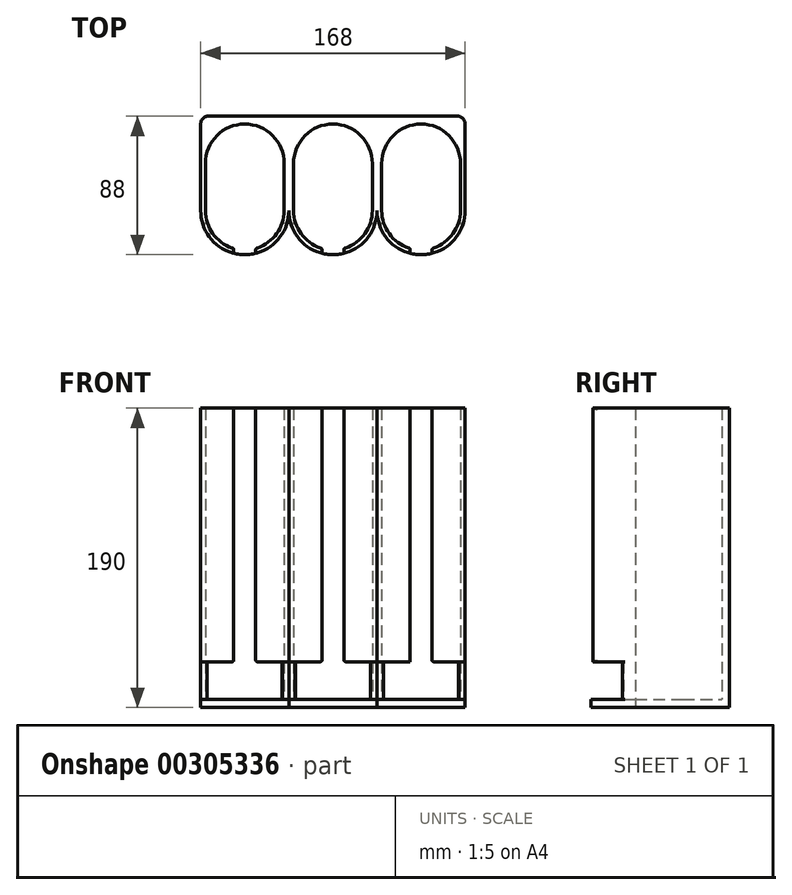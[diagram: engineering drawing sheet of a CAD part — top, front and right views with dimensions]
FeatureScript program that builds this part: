
annotation { "Feature Type Name" : "Feature", "Feature Type Description" : "" }
export const myFeature = defineFeature(function(context is Context, id is Id, definition is map)
    precondition{}
    {
        {
            var Q0;
            Q0=qCreatedBy(makeId("Top.planeOp"),FACE);
            var sketch = newSketch(context, id + "F0", { "sketchPlane" : qUnion([Q0])});
            skArc(sketch, "E0", {"start": v(-34.38, 12.6) * mm, "mid": v(-59.38, 37.6) * mm, "end": v(-84.38, 12.6) * mm});
            skLineSegment(sketch, "E1.left", {"start": v(-84.38, 12.6) * mm, "end": v(-84.38, -17.4) * mm});
            skLineSegment(sketch, "E1.right", {"start": v(-34.38, 12.6) * mm, "end": v(-34.38, -17.4) * mm});
            skArc(sketch, "E2", {"start": v(-84.38, -17.4) * mm, "mid": v(-59.38, -42.4) * mm, "end": v(-34.38, -17.4) * mm});
            skArc(sketch, "E3.2", {"start": v(-87.38, -17.4) * mm, "mid": v(-59.38, -45.4) * mm, "end": v(-31.38, -17.4) * mm});
            skLineSegment(sketch, "E3.3", {"start": v(-87.38, 12.6) * mm, "end": v(-87.38, -17.4) * mm});
            skLineSegment(sketch, "E4.bottom", {"start": v(-66.38, -40.37) * mm, "end": v(-52.38, -40.37) * mm});
            skLineSegment(sketch, "E4.top", {"start": v(-66.38, -47.03) * mm, "end": v(-52.38, -47.03) * mm});
            skLineSegment(sketch, "E4.left", {"start": v(-66.38, -40.37) * mm, "end": v(-66.38, -47.03) * mm});
            skLineSegment(sketch, "E4.right", {"start": v(-52.38, -40.37) * mm, "end": v(-52.38, -47.03) * mm});
            skArc(sketch, "E5", {"start": v(21.62, 12.6) * mm, "mid": v(-3.38, 37.6) * mm, "end": v(-28.38, 12.6) * mm});
            skLineSegment(sketch, "E6.left", {"start": v(-28.38, 12.6) * mm, "end": v(-28.38, -17.4) * mm});
            skLineSegment(sketch, "E6.right", {"start": v(21.62, 12.6) * mm, "end": v(21.62, -17.4) * mm});
            skArc(sketch, "E7", {"start": v(-28.38, -17.4) * mm, "mid": v(-3.38, -42.4) * mm, "end": v(21.62, -17.4) * mm});
            skArc(sketch, "E8.2", {"start": v(-31.38, -17.4) * mm, "mid": v(-3.38, -45.4) * mm, "end": v(24.62, -17.4) * mm});
            skLineSegment(sketch, "E9.bottom", {"start": v(-10.38, -40.37) * mm, "end": v(3.62, -40.37) * mm});
            skLineSegment(sketch, "E9.top", {"start": v(-10.38, -47.03) * mm, "end": v(3.62, -47.03) * mm});
            skLineSegment(sketch, "E9.left", {"start": v(-10.38, -40.37) * mm, "end": v(-10.38, -47.03) * mm});
            skLineSegment(sketch, "E9.right", {"start": v(3.62, -40.37) * mm, "end": v(3.62, -47.03) * mm});
            skArc(sketch, "E10", {"start": v(77.62, 12.6) * mm, "mid": v(52.62, 37.6) * mm, "end": v(27.62, 12.6) * mm});
            skLineSegment(sketch, "E11.left", {"start": v(27.62, 12.6) * mm, "end": v(27.62, -17.4) * mm});
            skLineSegment(sketch, "E11.right", {"start": v(77.62, 12.6) * mm, "end": v(77.62, -17.4) * mm});
            skArc(sketch, "E12", {"start": v(27.62, -17.4) * mm, "mid": v(52.62, -42.4) * mm, "end": v(77.62, -17.4) * mm});
            skLineSegment(sketch, "E13.1", {"start": v(80.62, 12.6) * mm, "end": v(80.62, -17.4) * mm});
            skArc(sketch, "E13.2", {"start": v(24.62, -17.4) * mm, "mid": v(52.62, -45.4) * mm, "end": v(80.62, -17.4) * mm});
            skLineSegment(sketch, "E14.bottom", {"start": v(45.62, -40.37) * mm, "end": v(59.62, -40.37) * mm});
            skLineSegment(sketch, "E14.top", {"start": v(45.62, -47.03) * mm, "end": v(59.62, -47.03) * mm});
            skLineSegment(sketch, "E14.left", {"start": v(45.62, -40.37) * mm, "end": v(45.62, -47.03) * mm});
            skLineSegment(sketch, "E14.right", {"start": v(59.62, -40.37) * mm, "end": v(59.62, -47.03) * mm});
            skLineSegment(sketch, "E15.top", {"start": v(-87.38, 42.6) * mm, "end": v(80.62, 42.6) * mm});
            skLineSegment(sketch, "E15.left", {"start": v(-87.38, 12.6) * mm, "end": v(-87.38, 42.6) * mm});
            skLineSegment(sketch, "E15.right", {"start": v(80.62, 12.6) * mm, "end": v(80.62, 42.6) * mm});
            skSolve(sketch);
        }
        {
            var Q0;
            {var subQ12=sQuery(id+"F0.wireOp",EDGE,"UXST9EkZ-4u4J-23rq-pVFZ-gqdFsX49M8eS.top");Q0=makeQuery(id+"F0.imprint","IMPRINT",FACE,{"disambiguationData":[TD([[makeQuery(id+"F0.imprint","IMPRINT",EDGE,{"derivedFrom":subQ12}),1.0]])]});}
            var Q1;
            {var subQ6=sQuery(id+"F0.wireOp",EDGE,"kwWkXOk3-viDk-uDqX-hwdr-6UO5nTlNDtKJ");Q1=makeQuery(id+"F0.imprint","IMPRINT",FACE,{"disambiguationData":[TD([[makeQuery(id+"F0.imprint","IMPRINT",EDGE,{"derivedFrom":subQ6}),-1.0]])]});}
            var Q2;
            {var subQ0=sQuery(id+"F0.wireOp",EDGE,"kwWkXOk3-viDk-uDqX-hwdr-6UO5nTlNDtKJ");Q2=makeQuery(id+"F0.imprint","IMPRINT",FACE,{"disambiguationData":[TD([[makeQuery(id+"F0.imprint","IMPRINT",EDGE,{"derivedFrom":subQ0}),1.0]])]});}
            var Q3;
            {var subQ5=sQuery(id+"F0.wireOp",EDGE,"a4c4f6ce-adb7-4228-82a1-ecae965dd3bb.0");var subQ7=sQuery(id+"F0.wireOp",EDGE,"a4c4f6ce-adb7-4228-82a1-ecae965dd3bb.3");var subQ8=makeQuery(id+"F0.imprint","INTERSECT",VERTEX,{"derivedFrom":[subQ5,subQ7]});Q3=makeQuery(id+"F0.imprint","IMPRINT",FACE,{"disambiguationData":[TD([[makeQuery(id+"F0.imprint","IMPRINT",EDGE,{"disambiguationData":[TD([[subQ8,1.0]])],"derivedFrom":subQ5}),1.0]])]});}
            var Q4;
            {var subQ8=sQuery(id+"F0.wireOp",EDGE,"a4c4f6ce-adb7-4228-82a1-ecae965dd3bb.0");var subQ11=sQuery(id+"F0.wireOp",EDGE,"a4c4f6ce-adb7-4228-82a1-ecae965dd3bb.3");var subQ12=makeQuery(id+"F0.imprint","INTERSECT",VERTEX,{"derivedFrom":[subQ8,subQ11]});Q4=makeQuery(id+"F0.imprint","IMPRINT",FACE,{"disambiguationData":[TD([[makeQuery(id+"F0.imprint","IMPRINT",EDGE,{"disambiguationData":[TD([[subQ12,1.0]])],"derivedFrom":subQ8}),-1.0]])]});}
            var Q5;
            {var subQ0=sQuery(id+"F0.wireOp",EDGE,"96b1cbd4-130d-4a2d-9362-919a265e6331.right");var subQ1=sQuery(id+"F0.wireOp",EDGE,"45cc61fa-5a03-413e-84e5-3475a93230b5");var subQ2=makeQuery(id+"F0.imprint","INTERSECT",VERTEX,{"derivedFrom":[subQ1,subQ0]});Q5=makeQuery(id+"F0.imprint","IMPRINT",FACE,{"disambiguationData":[TD([[makeQuery(id+"F0.imprint","IMPRINT",EDGE,{"disambiguationData":[TD([[subQ2,-1.0]])],"derivedFrom":subQ1}),1.0]])]});}
            var Q6;
            {var subQ5=sQuery(id+"F0.wireOp",EDGE,"E3.0");var subQ6=sQuery(id+"F0.wireOp",EDGE,"45cc61fa-5a03-413e-84e5-3475a93230b5");var subQ7=makeQuery(id+"F0.imprint","INTERSECT",VERTEX,{"derivedFrom":[subQ6,subQ5]});Q6=makeQuery(id+"F0.imprint","IMPRINT",FACE,{"disambiguationData":[TD([[makeQuery(id+"F0.imprint","IMPRINT",EDGE,{"disambiguationData":[TD([[subQ7,-1.0]])],"derivedFrom":subQ6}),-1.0]])]});}
            var Q7;
            {var subQ0=sQuery(id+"F0.wireOp",EDGE,"E0");var subQ1=sQuery(id+"F0.wireOp",EDGE,"855d7c93-3dc1-4a9f-ad3a-edb05c3c6de2.0");var subQ2=makeQuery(id+"F0.imprint","INTERSECT",VERTEX,{"derivedFrom":[subQ1,subQ0]});Q7=makeQuery(id+"F0.imprint","IMPRINT",FACE,{"disambiguationData":[TD([[makeQuery(id+"F0.imprint","IMPRINT",EDGE,{"disambiguationData":[TD([[subQ2,-1.0]])],"derivedFrom":subQ1}),-1.0]])]});}
            var Q8;
            {var subQ3=sQuery(id+"F0.wireOp",EDGE,"855d7c93-3dc1-4a9f-ad3a-edb05c3c6de2.0");var subQ6=sQuery(id+"F0.wireOp",EDGE,"E3.0");var subQ8=makeQuery(id+"F0.imprint","INTERSECT",VERTEX,{"derivedFrom":[subQ3,subQ6]});Q8=makeQuery(id+"F0.imprint","IMPRINT",FACE,{"disambiguationData":[TD([[makeQuery(id+"F0.imprint","IMPRINT",EDGE,{"disambiguationData":[TD([[subQ8,-1.0]])],"derivedFrom":subQ3}),-1.0]])]});}
            var Q9;
            {var subQ1=sQuery(id+"F0.wireOp",EDGE,"96b1cbd4-130d-4a2d-9362-919a265e6331.left");Q9=makeQuery(id+"F0.imprint","IMPRINT",FACE,{"disambiguationData":[TD([[makeQuery(id+"F0.imprint","IMPRINT",EDGE,{"derivedFrom":subQ1}),-1.0]])]});}
            var Q10;
            {var subQ7=sQuery(id+"F0.wireOp",EDGE,"E2");var subQ8=sQuery(id+"F0.wireOp",EDGE,"E1.left");var subQ9=makeQuery(id+"F0.imprint","INTERSECT",VERTEX,{"derivedFrom":[subQ8,subQ7]});Q10=makeQuery(id+"F0.imprint","IMPRINT",FACE,{"disambiguationData":[TD([[makeQuery(id+"F0.imprint","IMPRINT",EDGE,{"disambiguationData":[TD([[subQ9,1.0]])],"derivedFrom":subQ8}),-1.0]])]});}
            var Q11;
            {var subQ10=sQuery(id+"F0.wireOp",EDGE,"855d7c93-3dc1-4a9f-ad3a-edb05c3c6de2.3");Q11=makeQuery(id+"F0.imprint","IMPRINT",FACE,{"disambiguationData":[TD([[makeQuery(id+"F0.imprint","IMPRINT",EDGE,{"derivedFrom":subQ10}),-1.0]])]});}
            var Q12;
            {var subQ5=sQuery(id+"F0.wireOp",EDGE,"E4.bottom");Q12=makeQuery(id+"F0.imprint","IMPRINT",FACE,{"disambiguationData":[TD([[makeQuery(id+"F0.imprint","IMPRINT",EDGE,{"derivedFrom":subQ5}),-1.0]])]});}
            var Q13;
            {var subQ0=sQuery(id+"F0.wireOp",EDGE,"E3.2");var subQ1=sQuery(id+"F0.wireOp",EDGE,"855d7c93-3dc1-4a9f-ad3a-edb05c3c6de2.2");var subQ2=makeQuery(id+"F0.imprint","INTERSECT",VERTEX,{"derivedFrom":[subQ1,subQ0]});Q13=makeQuery(id+"F0.imprint","IMPRINT",FACE,{"disambiguationData":[TD([[makeQuery(id+"F0.imprint","IMPRINT",EDGE,{"disambiguationData":[TD([[subQ2,1.0]])],"derivedFrom":subQ1}),-1.0]])]});}
            var Q14;
            {var subQ6=sQuery(id+"F0.wireOp",EDGE,"o4JAiXg9-DfQB-Lprr-swcd-07qpl5tI4RPW.bottom");Q14=makeQuery(id+"F0.imprint","IMPRINT",FACE,{"disambiguationData":[TD([[makeQuery(id+"F0.imprint","IMPRINT",EDGE,{"derivedFrom":subQ6}),1.0]])]});}
            var Q15;
            {var subQ1=sQuery(id+"F0.wireOp",EDGE,"E3.1");var subQ5=sQuery(id+"F0.wireOp",EDGE,"d6663e3e-9dfa-41b2-b02d-e6aec3a7e438");var subQ6=makeQuery(id+"F0.imprint","INTERSECT",VERTEX,{"derivedFrom":[subQ5,subQ1]});Q15=makeQuery(id+"F0.imprint","IMPRINT",FACE,{"disambiguationData":[TD([[makeQuery(id+"F0.imprint","IMPRINT",EDGE,{"disambiguationData":[TD([[subQ6,-1.0]])],"derivedFrom":subQ5}),-1.0]])]});}
            var Q16;
            {var subQ5=sQuery(id+"F0.wireOp",EDGE,"o4JAiXg9-DfQB-Lprr-swcd-07qpl5tI4RPW.bottom");Q16=makeQuery(id+"F0.imprint","IMPRINT",FACE,{"disambiguationData":[TD([[makeQuery(id+"F0.imprint","IMPRINT",EDGE,{"derivedFrom":subQ5}),-1.0]])]});}
            var Q17;
            {var subQ0=sQuery(id+"F0.wireOp",EDGE,"o4JAiXg9-DfQB-Lprr-swcd-07qpl5tI4RPW.left");var subQ1=sQuery(id+"F0.wireOp",EDGE,"d6663e3e-9dfa-41b2-b02d-e6aec3a7e438");var subQ2=makeQuery(id+"F0.imprint","INTERSECT",VERTEX,{"derivedFrom":[subQ1,subQ0]});Q17=makeQuery(id+"F0.imprint","IMPRINT",FACE,{"disambiguationData":[TD([[makeQuery(id+"F0.imprint","IMPRINT",EDGE,{"disambiguationData":[TD([[subQ2,-1.0]])],"derivedFrom":subQ1}),-1.0]])]});}
            var Q18;
            {var subQ5=sQuery(id+"F0.wireOp",EDGE,"a4c4f6ce-adb7-4228-82a1-ecae965dd3bb.3");var subQ6=sQuery(id+"F0.wireOp",EDGE,"a4c4f6ce-adb7-4228-82a1-ecae965dd3bb.2");var subQ7=makeQuery(id+"F0.imprint","INTERSECT",VERTEX,{"derivedFrom":[subQ6,subQ5]});Q18=makeQuery(id+"F0.imprint","IMPRINT",FACE,{"disambiguationData":[TD([[makeQuery(id+"F0.imprint","IMPRINT",EDGE,{"disambiguationData":[TD([[subQ7,-1.0]])],"derivedFrom":subQ6}),-1.0]])]});}
            var Q19;
            {var subQ3=sQuery(id+"F0.wireOp",EDGE,"a4c4f6ce-adb7-4228-82a1-ecae965dd3bb.2");var subQ7=sQuery(id+"F0.wireOp",EDGE,"a4c4f6ce-adb7-4228-82a1-ecae965dd3bb.3");var subQ8=makeQuery(id+"F0.imprint","INTERSECT",VERTEX,{"derivedFrom":[subQ3,subQ7]});Q19=makeQuery(id+"F0.imprint","IMPRINT",FACE,{"disambiguationData":[TD([[makeQuery(id+"F0.imprint","IMPRINT",EDGE,{"disambiguationData":[TD([[subQ8,-1.0]])],"derivedFrom":subQ3}),1.0]])]});}
            var Q20;
            {var subQ5=sQuery(id+"F0.wireOp",EDGE,"zHXG1qvy-AbRm-SIj7-NfRi-9Sy5astTL28w");var subQ6=sQuery(id+"F0.wireOp",EDGE,"nXfFn5N0-6Buh-Se6b-7rvE-6La1GT5WE5c2.left");var subQ7=makeQuery(id+"F0.imprint","INTERSECT",VERTEX,{"derivedFrom":[subQ6,subQ5]});Q20=makeQuery(id+"F0.imprint","IMPRINT",FACE,{"disambiguationData":[TD([[makeQuery(id+"F0.imprint","IMPRINT",EDGE,{"disambiguationData":[TD([[subQ7,1.0]])],"derivedFrom":subQ6}),-1.0]])]});}
            var Q21;
            {var subQ0=sQuery(id+"F0.wireOp",EDGE,"kCUj0TKU-8dMh-rkvJ-Fl4E-ZpoXySVFhUaY.left");var subQ1=sQuery(id+"F0.wireOp",EDGE,"zHXG1qvy-AbRm-SIj7-NfRi-9Sy5astTL28w");var subQ2=makeQuery(id+"F0.imprint","INTERSECT",VERTEX,{"derivedFrom":[subQ1,subQ0]});Q21=makeQuery(id+"F0.imprint","IMPRINT",FACE,{"disambiguationData":[TD([[makeQuery(id+"F0.imprint","IMPRINT",EDGE,{"disambiguationData":[TD([[subQ2,-1.0]])],"derivedFrom":subQ1}),-1.0]])]});}
            var Q22;
            {var subQ0=sQuery(id+"F0.wireOp",EDGE,"a4c4f6ce-adb7-4228-82a1-ecae965dd3bb.1");Q22=makeQuery(id+"F0.imprint","IMPRINT",FACE,{"disambiguationData":[TD([[makeQuery(id+"F0.imprint","IMPRINT",EDGE,{"derivedFrom":subQ0}),-1.0]])]});}
            var Q23;
            {var subQ9=sQuery(id+"F0.wireOp",EDGE,"kCUj0TKU-8dMh-rkvJ-Fl4E-ZpoXySVFhUaY.bottom");Q23=makeQuery(id+"F0.imprint","IMPRINT",FACE,{"disambiguationData":[TD([[makeQuery(id+"F0.imprint","IMPRINT",EDGE,{"derivedFrom":subQ9}),1.0]])]});}
            var Q24;
            {var subQ5=sQuery(id+"F0.wireOp",EDGE,"kCUj0TKU-8dMh-rkvJ-Fl4E-ZpoXySVFhUaY.bottom");Q24=makeQuery(id+"F0.imprint","IMPRINT",FACE,{"disambiguationData":[TD([[makeQuery(id+"F0.imprint","IMPRINT",EDGE,{"derivedFrom":subQ5}),-1.0]])]});}
            var Q25;
            {var subQ0=sQuery(id+"F0.wireOp",EDGE,"E0");Q25=makeQuery(id+"F0.imprint","IMPRINT",FACE,{"disambiguationData":[TD([[makeQuery(id+"F0.imprint","IMPRINT",EDGE,{"derivedFrom":subQ0}),-1.0]])]});}
            var Q26;
            {var subQ5=sQuery(id+"F0.wireOp",EDGE,"E1.right");Q26=makeQuery(id+"F0.imprint","IMPRINT",FACE,{"disambiguationData":[TD([[makeQuery(id+"F0.imprint","IMPRINT",EDGE,{"derivedFrom":subQ5}),1.0]])]});}
            var Q27;
            {var subQ5=sQuery(id+"F0.wireOp",EDGE,"E6.left");Q27=makeQuery(id+"F0.imprint","IMPRINT",FACE,{"disambiguationData":[TD([[makeQuery(id+"F0.imprint","IMPRINT",EDGE,{"derivedFrom":subQ5}),-1.0]])]});}
            var Q28;
            {var subQ0=sQuery(id+"F0.wireOp",EDGE,"E5");Q28=makeQuery(id+"F0.imprint","IMPRINT",FACE,{"disambiguationData":[TD([[makeQuery(id+"F0.imprint","IMPRINT",EDGE,{"derivedFrom":subQ0}),-1.0]])]});}
            var Q29;
            {var subQ5=sQuery(id+"F0.wireOp",EDGE,"E6.right");Q29=makeQuery(id+"F0.imprint","IMPRINT",FACE,{"disambiguationData":[TD([[makeQuery(id+"F0.imprint","IMPRINT",EDGE,{"derivedFrom":subQ5}),1.0]])]});}
            var Q30;
            {var subQ5=sQuery(id+"F0.wireOp",EDGE,"E11.left");Q30=makeQuery(id+"F0.imprint","IMPRINT",FACE,{"disambiguationData":[TD([[makeQuery(id+"F0.imprint","IMPRINT",EDGE,{"derivedFrom":subQ5}),-1.0]])]});}
            var Q31;
            {var subQ0=sQuery(id+"F0.wireOp",EDGE,"E10");Q31=makeQuery(id+"F0.imprint","IMPRINT",FACE,{"disambiguationData":[TD([[makeQuery(id+"F0.imprint","IMPRINT",EDGE,{"derivedFrom":subQ0}),-1.0]])]});}
            var Q32;
            {var subQ5=sQuery(id+"F0.wireOp",EDGE,"E11.right");Q32=makeQuery(id+"F0.imprint","IMPRINT",FACE,{"disambiguationData":[TD([[makeQuery(id+"F0.imprint","IMPRINT",EDGE,{"derivedFrom":subQ5}),1.0]])]});}
            var Q33;
            {var subQ0=sQuery(id+"F0.wireOp",EDGE,"E4.left");var subQ1=sQuery(id+"F0.wireOp",EDGE,"E2");var subQ2=makeQuery(id+"F0.imprint","INTERSECT",VERTEX,{"derivedFrom":[subQ1,subQ0]});Q33=makeQuery(id+"F0.imprint","IMPRINT",FACE,{"disambiguationData":[TD([[makeQuery(id+"F0.imprint","IMPRINT",EDGE,{"disambiguationData":[TD([[subQ2,-1.0]])],"derivedFrom":subQ1}),-1.0]])]});}
            var Q34;
            {var subQ7=sQuery(id+"F0.wireOp",EDGE,"E1.left");Q34=makeQuery(id+"F0.imprint","IMPRINT",FACE,{"disambiguationData":[TD([[makeQuery(id+"F0.imprint","IMPRINT",EDGE,{"derivedFrom":subQ7}),1.0]])]});}
            var Q35;
            {var subQ4=sQuery(id+"F0.wireOp",EDGE,"E6.left");Q35=makeQuery(id+"F0.imprint","IMPRINT",FACE,{"disambiguationData":[TD([[makeQuery(id+"F0.imprint","IMPRINT",EDGE,{"derivedFrom":subQ4}),1.0]])]});}
            var Q36;
            {var subQ5=sQuery(id+"F0.wireOp",EDGE,"E9.bottom");Q36=makeQuery(id+"F0.imprint","IMPRINT",FACE,{"disambiguationData":[TD([[makeQuery(id+"F0.imprint","IMPRINT",EDGE,{"derivedFrom":subQ5}),-1.0]])]});}
            var Q37;
            {var subQ0=sQuery(id+"F0.wireOp",EDGE,"E9.left");var subQ1=sQuery(id+"F0.wireOp",EDGE,"E7");var subQ2=makeQuery(id+"F0.imprint","INTERSECT",VERTEX,{"derivedFrom":[subQ1,subQ0]});Q37=makeQuery(id+"F0.imprint","IMPRINT",FACE,{"disambiguationData":[TD([[makeQuery(id+"F0.imprint","IMPRINT",EDGE,{"disambiguationData":[TD([[subQ2,-1.0]])],"derivedFrom":subQ1}),-1.0]])]});}
            var Q38;
            {var subQ0=sQuery(id+"F0.wireOp",EDGE,"E0");Q38=makeQuery(id+"F0.imprint","IMPRINT",FACE,{"disambiguationData":[TD([[makeQuery(id+"F0.imprint","IMPRINT",EDGE,{"derivedFrom":subQ0}),1.0]])]});}
            var Q39;
            {var subQ0=sQuery(id+"F0.wireOp",EDGE,"E5");Q39=makeQuery(id+"F0.imprint","IMPRINT",FACE,{"disambiguationData":[TD([[makeQuery(id+"F0.imprint","IMPRINT",EDGE,{"derivedFrom":subQ0}),1.0]])]});}
            var Q40;
            {var subQ0=sQuery(id+"F0.wireOp",EDGE,"E10");Q40=makeQuery(id+"F0.imprint","IMPRINT",FACE,{"disambiguationData":[TD([[makeQuery(id+"F0.imprint","IMPRINT",EDGE,{"derivedFrom":subQ0}),1.0]])]});}
            var Q41;
            {var subQ4=sQuery(id+"F0.wireOp",EDGE,"E11.left");Q41=makeQuery(id+"F0.imprint","IMPRINT",FACE,{"disambiguationData":[TD([[makeQuery(id+"F0.imprint","IMPRINT",EDGE,{"derivedFrom":subQ4}),1.0]])]});}
            var Q42;
            {var subQ5=sQuery(id+"F0.wireOp",EDGE,"E14.bottom");Q42=makeQuery(id+"F0.imprint","IMPRINT",FACE,{"disambiguationData":[TD([[makeQuery(id+"F0.imprint","IMPRINT",EDGE,{"derivedFrom":subQ5}),-1.0]])]});}
            var Q43;
            {var subQ0=sQuery(id+"F0.wireOp",EDGE,"E14.left");var subQ1=sQuery(id+"F0.wireOp",EDGE,"E12");var subQ2=makeQuery(id+"F0.imprint","INTERSECT",VERTEX,{"derivedFrom":[subQ1,subQ0]});Q43=makeQuery(id+"F0.imprint","IMPRINT",FACE,{"disambiguationData":[TD([[makeQuery(id+"F0.imprint","IMPRINT",EDGE,{"disambiguationData":[TD([[subQ2,-1.0]])],"derivedFrom":subQ1}),-1.0]])]});}
            extrude(context, id + "F1", {"entities" : qUnion([Q0, Q1, Q2, Q3, Q4, Q5, Q6, Q7, Q8, Q9, Q10, Q11, Q12, Q13, Q14, Q15, Q16, Q17, Q18, Q19, Q20, Q21, Q22, Q23, Q24, Q25, Q26, Q27, Q28, Q29, Q30, Q31, Q32, Q33, Q34, Q35, Q36, Q37, Q38, Q39, Q40, Q41, Q42, Q43]), "depth" : 5 * mm});
        }
        {
            var Q0;
            {var subQ0=sQuery(id+"F0.wireOp",EDGE,"a4c4f6ce-adb7-4228-82a1-ecae965dd3bb.1");Q0=makeQuery(id+"F0.imprint","IMPRINT",FACE,{"disambiguationData":[TD([[makeQuery(id+"F0.imprint","IMPRINT",EDGE,{"derivedFrom":subQ0}),-1.0]])]});}
            var Q1;
            {var subQ6=sQuery(id+"F0.wireOp",EDGE,"kwWkXOk3-viDk-uDqX-hwdr-6UO5nTlNDtKJ");Q1=makeQuery(id+"F0.imprint","IMPRINT",FACE,{"disambiguationData":[TD([[makeQuery(id+"F0.imprint","IMPRINT",EDGE,{"derivedFrom":subQ6}),-1.0]])]});}
            var Q2;
            {var subQ5=sQuery(id+"F0.wireOp",EDGE,"zHXG1qvy-AbRm-SIj7-NfRi-9Sy5astTL28w");var subQ6=sQuery(id+"F0.wireOp",EDGE,"nXfFn5N0-6Buh-Se6b-7rvE-6La1GT5WE5c2.left");var subQ7=makeQuery(id+"F0.imprint","INTERSECT",VERTEX,{"derivedFrom":[subQ6,subQ5]});Q2=makeQuery(id+"F0.imprint","IMPRINT",FACE,{"disambiguationData":[TD([[makeQuery(id+"F0.imprint","IMPRINT",EDGE,{"disambiguationData":[TD([[subQ7,1.0]])],"derivedFrom":subQ6}),-1.0]])]});}
            var Q3;
            {var subQ5=sQuery(id+"F0.wireOp",EDGE,"a4c4f6ce-adb7-4228-82a1-ecae965dd3bb.3");var subQ6=sQuery(id+"F0.wireOp",EDGE,"a4c4f6ce-adb7-4228-82a1-ecae965dd3bb.2");var subQ7=makeQuery(id+"F0.imprint","INTERSECT",VERTEX,{"derivedFrom":[subQ6,subQ5]});Q3=makeQuery(id+"F0.imprint","IMPRINT",FACE,{"disambiguationData":[TD([[makeQuery(id+"F0.imprint","IMPRINT",EDGE,{"disambiguationData":[TD([[subQ7,-1.0]])],"derivedFrom":subQ6}),-1.0]])]});}
            var Q4;
            {var subQ3=sQuery(id+"F0.wireOp",EDGE,"a4c4f6ce-adb7-4228-82a1-ecae965dd3bb.2");var subQ7=sQuery(id+"F0.wireOp",EDGE,"a4c4f6ce-adb7-4228-82a1-ecae965dd3bb.3");var subQ8=makeQuery(id+"F0.imprint","INTERSECT",VERTEX,{"derivedFrom":[subQ3,subQ7]});Q4=makeQuery(id+"F0.imprint","IMPRINT",FACE,{"disambiguationData":[TD([[makeQuery(id+"F0.imprint","IMPRINT",EDGE,{"disambiguationData":[TD([[subQ8,-1.0]])],"derivedFrom":subQ3}),1.0]])]});}
            var Q5;
            {var subQ5=sQuery(id+"F0.wireOp",EDGE,"a4c4f6ce-adb7-4228-82a1-ecae965dd3bb.0");var subQ7=sQuery(id+"F0.wireOp",EDGE,"a4c4f6ce-adb7-4228-82a1-ecae965dd3bb.3");var subQ8=makeQuery(id+"F0.imprint","INTERSECT",VERTEX,{"derivedFrom":[subQ5,subQ7]});Q5=makeQuery(id+"F0.imprint","IMPRINT",FACE,{"disambiguationData":[TD([[makeQuery(id+"F0.imprint","IMPRINT",EDGE,{"disambiguationData":[TD([[subQ8,1.0]])],"derivedFrom":subQ5}),1.0]])]});}
            var Q6;
            {var subQ8=sQuery(id+"F0.wireOp",EDGE,"a4c4f6ce-adb7-4228-82a1-ecae965dd3bb.0");var subQ11=sQuery(id+"F0.wireOp",EDGE,"a4c4f6ce-adb7-4228-82a1-ecae965dd3bb.3");var subQ12=makeQuery(id+"F0.imprint","INTERSECT",VERTEX,{"derivedFrom":[subQ8,subQ11]});Q6=makeQuery(id+"F0.imprint","IMPRINT",FACE,{"disambiguationData":[TD([[makeQuery(id+"F0.imprint","IMPRINT",EDGE,{"disambiguationData":[TD([[subQ12,1.0]])],"derivedFrom":subQ8}),-1.0]])]});}
            var Q7;
            {var subQ1=sQuery(id+"F0.wireOp",EDGE,"E3.1");var subQ5=sQuery(id+"F0.wireOp",EDGE,"d6663e3e-9dfa-41b2-b02d-e6aec3a7e438");var subQ6=makeQuery(id+"F0.imprint","INTERSECT",VERTEX,{"derivedFrom":[subQ5,subQ1]});Q7=makeQuery(id+"F0.imprint","IMPRINT",FACE,{"disambiguationData":[TD([[makeQuery(id+"F0.imprint","IMPRINT",EDGE,{"disambiguationData":[TD([[subQ6,-1.0]])],"derivedFrom":subQ5}),-1.0]])]});}
            var Q8;
            {var subQ1=sQuery(id+"F0.wireOp",EDGE,"96b1cbd4-130d-4a2d-9362-919a265e6331.left");Q8=makeQuery(id+"F0.imprint","IMPRINT",FACE,{"disambiguationData":[TD([[makeQuery(id+"F0.imprint","IMPRINT",EDGE,{"derivedFrom":subQ1}),-1.0]])]});}
            var Q9;
            {var subQ0=sQuery(id+"F0.wireOp",EDGE,"E3.2");var subQ1=sQuery(id+"F0.wireOp",EDGE,"855d7c93-3dc1-4a9f-ad3a-edb05c3c6de2.2");var subQ2=makeQuery(id+"F0.imprint","INTERSECT",VERTEX,{"derivedFrom":[subQ1,subQ0]});Q9=makeQuery(id+"F0.imprint","IMPRINT",FACE,{"disambiguationData":[TD([[makeQuery(id+"F0.imprint","IMPRINT",EDGE,{"disambiguationData":[TD([[subQ2,1.0]])],"derivedFrom":subQ1}),-1.0]])]});}
            var Q10;
            {var subQ5=sQuery(id+"F0.wireOp",EDGE,"E3.0");var subQ6=sQuery(id+"F0.wireOp",EDGE,"45cc61fa-5a03-413e-84e5-3475a93230b5");var subQ7=makeQuery(id+"F0.imprint","INTERSECT",VERTEX,{"derivedFrom":[subQ6,subQ5]});Q10=makeQuery(id+"F0.imprint","IMPRINT",FACE,{"disambiguationData":[TD([[makeQuery(id+"F0.imprint","IMPRINT",EDGE,{"disambiguationData":[TD([[subQ7,-1.0]])],"derivedFrom":subQ6}),-1.0]])]});}
            var Q11;
            {var subQ3=sQuery(id+"F0.wireOp",EDGE,"855d7c93-3dc1-4a9f-ad3a-edb05c3c6de2.0");var subQ6=sQuery(id+"F0.wireOp",EDGE,"E3.0");var subQ8=makeQuery(id+"F0.imprint","INTERSECT",VERTEX,{"derivedFrom":[subQ3,subQ6]});Q11=makeQuery(id+"F0.imprint","IMPRINT",FACE,{"disambiguationData":[TD([[makeQuery(id+"F0.imprint","IMPRINT",EDGE,{"disambiguationData":[TD([[subQ8,-1.0]])],"derivedFrom":subQ3}),-1.0]])]});}
            var Q12;
            {var subQ7=sQuery(id+"F0.wireOp",EDGE,"E2");var subQ8=sQuery(id+"F0.wireOp",EDGE,"E1.left");var subQ9=makeQuery(id+"F0.imprint","INTERSECT",VERTEX,{"derivedFrom":[subQ8,subQ7]});Q12=makeQuery(id+"F0.imprint","IMPRINT",FACE,{"disambiguationData":[TD([[makeQuery(id+"F0.imprint","IMPRINT",EDGE,{"disambiguationData":[TD([[subQ9,1.0]])],"derivedFrom":subQ8}),-1.0]])]});}
            var Q13;
            {var subQ12=sQuery(id+"F0.wireOp",EDGE,"UXST9EkZ-4u4J-23rq-pVFZ-gqdFsX49M8eS.top");Q13=makeQuery(id+"F0.imprint","IMPRINT",FACE,{"disambiguationData":[TD([[makeQuery(id+"F0.imprint","IMPRINT",EDGE,{"derivedFrom":subQ12}),1.0]])]});}
            extrude(context, id + "F2", {"entities" : qUnion([Q0, Q1, Q2, Q3, Q4, Q5, Q6, Q7, Q8, Q9, Q10, Q11, Q12, Q13]), "operationType" : NewBodyOperationType.ADD, "depth" : 190 * mm});
        }
        {
            var Q0;
            Q0=qCreatedBy(makeId("Front.planeOp"),FACE);
            cPlane(context, id + "F3", {"entities" : qUnion([Q0]), "cplaneType" : CPlaneType.OFFSET, "offset" : 50 * mm, "width" : 150 * mm, "height" : 150 * mm});
        }
        {
            var Q0;
            Q0=qCreatedBy(id+"F3.planeOp",FACE);
            var sketch = newSketch(context, id + "F4", { "sketchPlane" : qUnion([Q0])});
            skLineSegment(sketch, "E16.bottom", {"start": v(-83.38, 29) * mm, "end": v(-35.38, 29) * mm});
            skLineSegment(sketch, "E16.top", {"start": v(-83.38, 5) * mm, "end": v(-35.38, 5) * mm});
            skLineSegment(sketch, "E16.left", {"start": v(-83.38, 29) * mm, "end": v(-83.38, 5) * mm});
            skLineSegment(sketch, "E16.right", {"start": v(-35.38, 29) * mm, "end": v(-35.38, 5) * mm});
            skLineSegment(sketch, "E17.bottom", {"start": v(20.62, 29) * mm, "end": v(-27.38, 29) * mm});
            skLineSegment(sketch, "E17.top", {"start": v(20.62, 5) * mm, "end": v(-27.38, 5) * mm});
            skLineSegment(sketch, "E17.left", {"start": v(-27.38, 29) * mm, "end": v(-27.38, 5) * mm});
            skLineSegment(sketch, "E17.right", {"start": v(20.62, 29) * mm, "end": v(20.62, 5) * mm});
            skLineSegment(sketch, "E18.bottom", {"start": v(28.62, 29) * mm, "end": v(76.62, 29) * mm});
            skLineSegment(sketch, "E18.top", {"start": v(28.62, 5) * mm, "end": v(76.62, 5) * mm});
            skLineSegment(sketch, "E18.left", {"start": v(28.62, 29) * mm, "end": v(28.62, 5) * mm});
            skLineSegment(sketch, "E18.right", {"start": v(76.62, 29) * mm, "end": v(76.62, 5) * mm});
            skSolve(sketch);
        }
        {
            var Q0;
            Q0=makeQuery(id+"F4.imprint","IMPRINT",FACE,{"disambiguationData":[TD([[makeQuery(id+"F4.imprint","IMPRINT",EDGE,{"derivedFrom":sQuery(id+"F4.wireOp",EDGE,"E16.bottom")}),-1.0]])]});
            var Q1;
            Q1=makeQuery(id+"F4.imprint","IMPRINT",FACE,{"disambiguationData":[TD([[makeQuery(id+"F4.imprint","IMPRINT",EDGE,{"derivedFrom":sQuery(id+"F4.wireOp",EDGE,"E17.bottom")}),1.0]])]});
            var Q2;
            Q2=makeQuery(id+"F4.imprint","IMPRINT",FACE,{"disambiguationData":[TD([[makeQuery(id+"F4.imprint","IMPRINT",EDGE,{"derivedFrom":sQuery(id+"F4.wireOp",EDGE,"E18.bottom")}),-1.0]])]});
            extrude(context, id + "F5", {"entities" : qUnion([Q0, Q1, Q2]), "operationType" : NewBodyOperationType.REMOVE, "oppositeDirection" : true, "depth" : 25 * mm});
        }
        {
            var Q0;
            {var subQ0=sQuery(id+"F0.wireOp",EDGE,"E15.left");var subQ1=sQuery(id+"F0.wireOp",EDGE,"E15.top");Q0=makeQuery(id+"F2.boolean.opBoolean","MERGE",EDGE,{"derivedFrom":[makeQuery(id+"F1.opExtrude","SWEPT_EDGE",EDGE,{"disambiguationData":[OSD([subQ1,subQ0])]}),makeQuery(id+"F2.opExtrude","SWEPT_EDGE",EDGE,{"disambiguationData":[OSD([subQ1,subQ0])]})]});}
            var Q1;
            {var subQ0=sQuery(id+"F0.wireOp",EDGE,"E15.right");var subQ1=sQuery(id+"F0.wireOp",EDGE,"E15.top");Q1=makeQuery(id+"F2.boolean.opBoolean","MERGE",EDGE,{"derivedFrom":[makeQuery(id+"F1.opExtrude","SWEPT_EDGE",EDGE,{"disambiguationData":[OSD([subQ1,subQ0])]}),makeQuery(id+"F2.opExtrude","SWEPT_EDGE",EDGE,{"disambiguationData":[OSD([subQ1,subQ0])]})]});}
            fillet(context, id + "F6", {"entities" : qUnion([Q0, Q1]), "radius" : 5 * mm, "tangentPropagation" : true, "allowEdgeOverflow" : false});
        }
        {
            var Q0;
            {var subQ0=sQuery(id+"F0.wireOp",EDGE,"E3.2");Q0=makeQuery(id+"F5.boolean.opBoolean","INTERSECT",EDGE,{"derivedFrom":[makeQuery(id+"F2.boolean.opBoolean","MERGE",FACE,{"derivedFrom":[makeQuery(id+"F1.opExtrude","SWEPT_FACE",FACE,{"disambiguationData":[OSD([subQ0])]}),makeQuery(id+"F2.opExtrude","SWEPT_FACE",FACE,{"disambiguationData":[OSD([subQ0]),TDD([makeQuery(id+"F0.imprint","IMPRINT",EDGE,{"disambiguationData":[TD([[makeQuery(id+"F0.imprint","INTERSECT",VERTEX,{"derivedFrom":[subQ0,sQuery(id+"F0.wireOp",EDGE,"E3.3")]}),-1.0]])],"derivedFrom":subQ0})])]}),makeQuery(id+"F2.opExtrude","SWEPT_FACE",FACE,{"disambiguationData":[OSD([subQ0]),TDD([makeQuery(id+"F0.imprint","IMPRINT",EDGE,{"disambiguationData":[TD([[makeQuery(id+"F0.imprint","INTERSECT",VERTEX,{"derivedFrom":[subQ0,sQuery(id+"F0.wireOp",EDGE,"E8.2")]}),1.0]])],"derivedFrom":subQ0})])]})]}),makeQuery(id+"F5.opExtrude","SWEPT_FACE",FACE,{"disambiguationData":[OSD([sQuery(id+"F4.wireOp",EDGE,"E16.left")])]})]});}
            var Q1;
            {var subQ0=sQuery(id+"F0.wireOp",EDGE,"E3.2");Q1=makeQuery(id+"F5.boolean.opBoolean","INTERSECT",EDGE,{"derivedFrom":[makeQuery(id+"F2.boolean.opBoolean","MERGE",FACE,{"derivedFrom":[makeQuery(id+"F1.opExtrude","SWEPT_FACE",FACE,{"disambiguationData":[OSD([subQ0])]}),makeQuery(id+"F2.opExtrude","SWEPT_FACE",FACE,{"disambiguationData":[OSD([subQ0]),TDD([makeQuery(id+"F0.imprint","IMPRINT",EDGE,{"disambiguationData":[TD([[makeQuery(id+"F0.imprint","INTERSECT",VERTEX,{"derivedFrom":[subQ0,sQuery(id+"F0.wireOp",EDGE,"E3.3")]}),-1.0]])],"derivedFrom":subQ0})])]}),makeQuery(id+"F2.opExtrude","SWEPT_FACE",FACE,{"disambiguationData":[OSD([subQ0]),TDD([makeQuery(id+"F0.imprint","IMPRINT",EDGE,{"disambiguationData":[TD([[makeQuery(id+"F0.imprint","INTERSECT",VERTEX,{"derivedFrom":[subQ0,sQuery(id+"F0.wireOp",EDGE,"E8.2")]}),1.0]])],"derivedFrom":subQ0})])]})]}),makeQuery(id+"F5.opExtrude","SWEPT_FACE",FACE,{"disambiguationData":[OSD([sQuery(id+"F4.wireOp",EDGE,"E16.right")])]})]});}
            var Q2;
            {var subQ0=sQuery(id+"F0.wireOp",EDGE,"E8.2");Q2=makeQuery(id+"F5.boolean.opBoolean","INTERSECT",EDGE,{"derivedFrom":[makeQuery(id+"F2.boolean.opBoolean","MERGE",FACE,{"derivedFrom":[makeQuery(id+"F1.opExtrude","SWEPT_FACE",FACE,{"disambiguationData":[OSD([subQ0])]}),makeQuery(id+"F2.opExtrude","SWEPT_FACE",FACE,{"disambiguationData":[OSD([subQ0]),TDD([makeQuery(id+"F0.imprint","IMPRINT",EDGE,{"disambiguationData":[TD([[makeQuery(id+"F0.imprint","INTERSECT",VERTEX,{"derivedFrom":[sQuery(id+"F0.wireOp",EDGE,"E3.2"),subQ0]}),-1.0]])],"derivedFrom":subQ0})])]}),makeQuery(id+"F2.opExtrude","SWEPT_FACE",FACE,{"disambiguationData":[OSD([subQ0]),TDD([makeQuery(id+"F0.imprint","IMPRINT",EDGE,{"disambiguationData":[TD([[makeQuery(id+"F0.imprint","INTERSECT",VERTEX,{"derivedFrom":[subQ0,sQuery(id+"F0.wireOp",EDGE,"E13.2")]}),1.0]])],"derivedFrom":subQ0})])]})]}),makeQuery(id+"F5.opExtrude","SWEPT_FACE",FACE,{"disambiguationData":[OSD([sQuery(id+"F4.wireOp",EDGE,"E17.left")])]})]});}
            var Q3;
            {var subQ0=sQuery(id+"F0.wireOp",EDGE,"E8.2");Q3=makeQuery(id+"F5.boolean.opBoolean","INTERSECT",EDGE,{"derivedFrom":[makeQuery(id+"F2.boolean.opBoolean","MERGE",FACE,{"derivedFrom":[makeQuery(id+"F1.opExtrude","SWEPT_FACE",FACE,{"disambiguationData":[OSD([subQ0])]}),makeQuery(id+"F2.opExtrude","SWEPT_FACE",FACE,{"disambiguationData":[OSD([subQ0]),TDD([makeQuery(id+"F0.imprint","IMPRINT",EDGE,{"disambiguationData":[TD([[makeQuery(id+"F0.imprint","INTERSECT",VERTEX,{"derivedFrom":[sQuery(id+"F0.wireOp",EDGE,"E3.2"),subQ0]}),-1.0]])],"derivedFrom":subQ0})])]}),makeQuery(id+"F2.opExtrude","SWEPT_FACE",FACE,{"disambiguationData":[OSD([subQ0]),TDD([makeQuery(id+"F0.imprint","IMPRINT",EDGE,{"disambiguationData":[TD([[makeQuery(id+"F0.imprint","INTERSECT",VERTEX,{"derivedFrom":[subQ0,sQuery(id+"F0.wireOp",EDGE,"E13.2")]}),1.0]])],"derivedFrom":subQ0})])]})]}),makeQuery(id+"F5.opExtrude","SWEPT_FACE",FACE,{"disambiguationData":[OSD([sQuery(id+"F4.wireOp",EDGE,"E17.right")])]})]});}
            var Q4;
            {var subQ0=sQuery(id+"F0.wireOp",EDGE,"E13.2");Q4=makeQuery(id+"F5.boolean.opBoolean","INTERSECT",EDGE,{"derivedFrom":[makeQuery(id+"F2.boolean.opBoolean","MERGE",FACE,{"derivedFrom":[makeQuery(id+"F1.opExtrude","SWEPT_FACE",FACE,{"disambiguationData":[OSD([subQ0])]}),makeQuery(id+"F2.opExtrude","SWEPT_FACE",FACE,{"disambiguationData":[OSD([subQ0]),TDD([makeQuery(id+"F0.imprint","IMPRINT",EDGE,{"disambiguationData":[TD([[makeQuery(id+"F0.imprint","INTERSECT",VERTEX,{"derivedFrom":[sQuery(id+"F0.wireOp",EDGE,"E8.2"),subQ0]}),-1.0]])],"derivedFrom":subQ0})])]}),makeQuery(id+"F2.opExtrude","SWEPT_FACE",FACE,{"disambiguationData":[OSD([subQ0]),TDD([makeQuery(id+"F0.imprint","IMPRINT",EDGE,{"disambiguationData":[TD([[makeQuery(id+"F0.imprint","INTERSECT",VERTEX,{"derivedFrom":[sQuery(id+"F0.wireOp",EDGE,"E13.1"),subQ0]}),1.0]])],"derivedFrom":subQ0})])]})]}),makeQuery(id+"F5.opExtrude","SWEPT_FACE",FACE,{"disambiguationData":[OSD([sQuery(id+"F4.wireOp",EDGE,"E18.right")])]})]});}
            var Q5;
            {var subQ0=sQuery(id+"F0.wireOp",EDGE,"E13.2");Q5=makeQuery(id+"F5.boolean.opBoolean","INTERSECT",EDGE,{"derivedFrom":[makeQuery(id+"F2.boolean.opBoolean","MERGE",FACE,{"derivedFrom":[makeQuery(id+"F1.opExtrude","SWEPT_FACE",FACE,{"disambiguationData":[OSD([subQ0])]}),makeQuery(id+"F2.opExtrude","SWEPT_FACE",FACE,{"disambiguationData":[OSD([subQ0]),TDD([makeQuery(id+"F0.imprint","IMPRINT",EDGE,{"disambiguationData":[TD([[makeQuery(id+"F0.imprint","INTERSECT",VERTEX,{"derivedFrom":[sQuery(id+"F0.wireOp",EDGE,"E8.2"),subQ0]}),-1.0]])],"derivedFrom":subQ0})])]}),makeQuery(id+"F2.opExtrude","SWEPT_FACE",FACE,{"disambiguationData":[OSD([subQ0]),TDD([makeQuery(id+"F0.imprint","IMPRINT",EDGE,{"disambiguationData":[TD([[makeQuery(id+"F0.imprint","INTERSECT",VERTEX,{"derivedFrom":[sQuery(id+"F0.wireOp",EDGE,"E13.1"),subQ0]}),1.0]])],"derivedFrom":subQ0})])]})]}),makeQuery(id+"F5.opExtrude","SWEPT_FACE",FACE,{"disambiguationData":[OSD([sQuery(id+"F4.wireOp",EDGE,"E18.left")])]})]});}
            fillet(context, id + "F7", {"entities" : qUnion([Q0, Q1, Q2, Q3, Q4, Q5]), "radius" : 2 * mm, "tangentPropagation" : true, "allowEdgeOverflow" : false});
        }
        {
            var Q0;
            Q0=makeQuery(id+"F2.opExtrude","SWEPT_FACE",FACE,{"disambiguationData":[OSD([sQuery(id+"F0.wireOp",EDGE,"E4.left")])]});
            var Q1;
            Q1=makeQuery(id+"F2.opExtrude","SWEPT_FACE",FACE,{"disambiguationData":[OSD([sQuery(id+"F0.wireOp",EDGE,"E4.right")])]});
            var Q2;
            Q2=makeQuery(id+"F2.opExtrude","SWEPT_FACE",FACE,{"disambiguationData":[OSD([sQuery(id+"F0.wireOp",EDGE,"E9.right")])]});
            var Q3;
            Q3=makeQuery(id+"F2.opExtrude","SWEPT_FACE",FACE,{"disambiguationData":[OSD([sQuery(id+"F0.wireOp",EDGE,"E14.right")])]});
            var Q4;
            Q4=makeQuery(id+"F2.opExtrude","SWEPT_EDGE",EDGE,{"disambiguationData":[OSD([sQuery(id+"F0.wireOp",EDGE,"E12"),sQuery(id+"F0.wireOp",EDGE,"E14.left")])]});
            var Q5;
            Q5=makeQuery(id+"F2.opExtrude","SWEPT_FACE",FACE,{"disambiguationData":[OSD([sQuery(id+"F0.wireOp",EDGE,"E9.left")])]});
            var Q6;
            Q6=makeQuery(id+"F2.opExtrude","SWEPT_EDGE",EDGE,{"disambiguationData":[OSD([sQuery(id+"F0.wireOp",EDGE,"E13.2"),sQuery(id+"F0.wireOp",EDGE,"E14.left")])]});
            fillet(context, id + "F8", {"entities" : qUnion([Q0, Q1, Q2, Q3, Q4, Q5, Q6]), "radius" : 1 * mm, "tangentPropagation" : true, "allowEdgeOverflow" : false});
        }
    });
